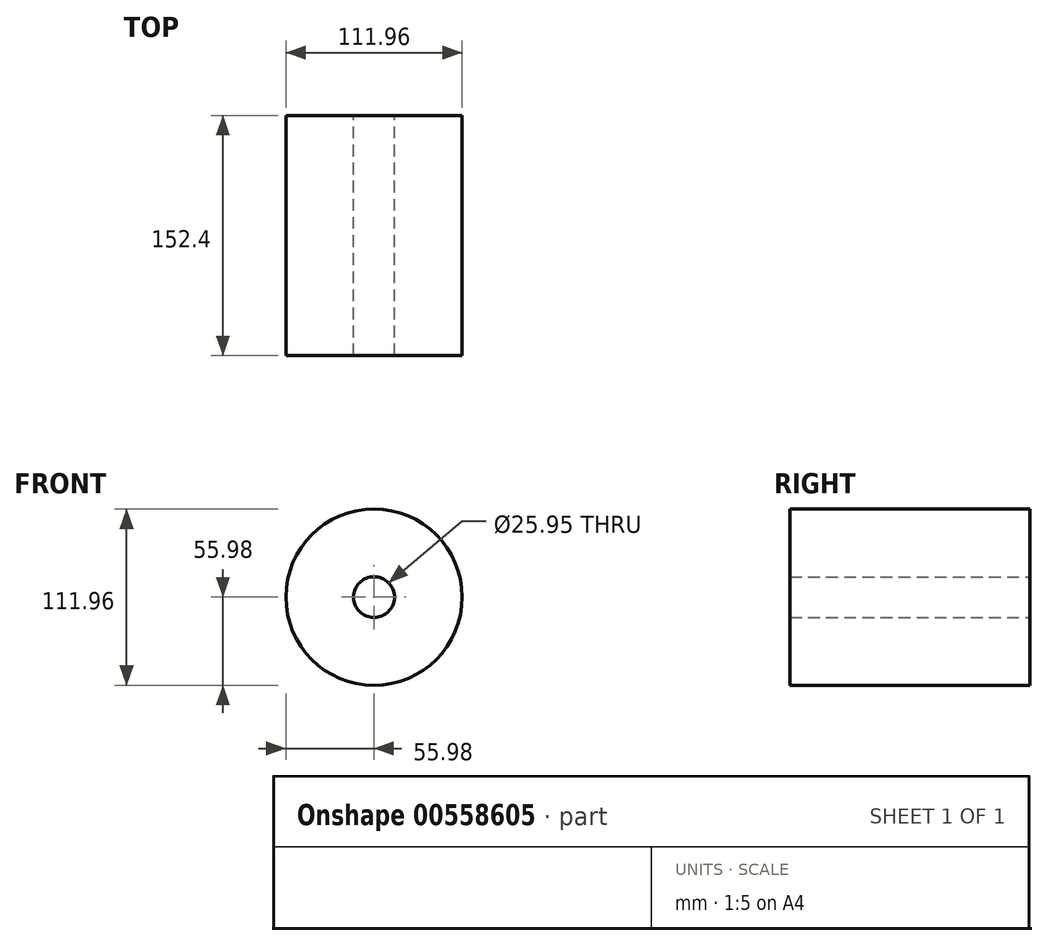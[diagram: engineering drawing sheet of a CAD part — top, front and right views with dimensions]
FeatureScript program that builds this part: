
annotation { "Feature Type Name" : "Feature", "Feature Type Description" : "" }
export const myFeature = defineFeature(function(context is Context, id is Id, definition is map)
    precondition{}
    {
        {
            var Q0;
            Q0=qCreatedBy(makeId("Front.planeOp"),FACE);
            var sketch = newSketch(context, id + "F0", { "sketchPlane" : qUnion([Q0])});
            skCircle(sketch, "E0", {"center": v(0, 0) * mm, "radius": 55.98 * mm});
            skCircle(sketch, "E1", {"center": v(0, 0) * mm, "radius": 12.97 * mm});
            skSolve(sketch);
        }
        {
            var Q0;
            Q0 = qSketchRegion(id + "F0", true);
            extrude(context, id + "F1", {"entities" : qUnion([Q0]), "depth" : 25.4 * mm, "offsetDistance" : 25.4 * mm});
        }
        {
            var Q0;
            Q0=makeQuery(id+"F1.opExtrude","CAP_FACE",FACE,{"disambiguationData":[OSD([sQuery(id+"F0.wireOp",EDGE,"E0"),sQuery(id+"F0.wireOp",EDGE,"E1")])],"isStart":false});
            var sketch = newSketch(context, id + "F2", { "sketchPlane" : qUnion([Q0])});
            skSolve(sketch);
        }
        {
            var Q0;
            Q0=makeQuery(id+"F2.imprint","IMPRINT",FACE,{"disambiguationData":[TD([[makeQuery(id+"F2.imprint","IMPRINT",EDGE,{"derivedFrom":makeQuery(id+"F1.opExtrude","CAP_EDGE",EDGE,{"disambiguationData":[OSD([sQuery(id+"F0.wireOp",EDGE,"E0")])],"isStart":false})}),1.0]])]});
            extrude(context, id + "F3", {"entities" : qUnion([Q0]), "operationType" : NewBodyOperationType.ADD, "depth" : 127 * mm, "offsetDistance" : 25.4 * mm});
        }
    });
